# Revit family: IS_Extra_BD510_BIM_GB
name_source: partatom
category: Plumbing Fixtures
units: mm (PartAtom-declared; Revit-internal decimal feet)

## family parameters
Always vertical = No
Cut with Voids When Loaded = No
OmniClass Number = 23.45.55.17
OmniClass Title = Mixing Faucets
Part Type = Normal
Room Calculation Point = No
Round Connector Dimension = Use Diameter
Shared = No
Work Plane-Based = No

## types (4) — shared parameters
BIMobject category = Taps & Mixers
BIMobject category code = sanitary-taps-mixers
BIMobject main category = Sanitary
BIMobject main category code = sanitary
Brand url = http://www.idealstandard.co.uk
Date of publishing = 09/11/2022
Description = Basin built in wall mounted 220mm kit 2 - for combination with kit 1 A1313NU
Edition number = 1
IFC Classification = Sanitary Terminal
Installation instructions = https://www.idealstandard.co.uk
Manufacturer = Ideal Standard
Manufacturer name = Ideal Standard
Masterformat 2014 Code = 22 40 00
Masterformat 2014 Description = Plumbing Fixtures
Material main = Brass
NBS Reference Code = 45-35-70/371
NBS Reference Description = Water supply fittings for wash basins and troughs
NominalHeight = 108 mm
NominalLength = 230 mm
NominalWidth = 167 mm
OmniClass Code = 23-31 11 00
OmniClass Description = Faucets
Product Guid = 95e05450-5292-4f1d-a68c-7bc8d674b562
Product SKU = BD510
Product certification = https://www.idealstandard.co.uk
Product data url = https://bimobject.com
Product family = Extra
Product group = Taps & Mixers
Product name = Basin built in wall mounted 220mm kit 2 - for combination with kit 1 A1313NU
Product url = https://www.idealstandard.co.uk
QR code = http://bimobject.com
Size = 167 x 230 x 108 mm
Technical description = https://www.idealstandard.co.uk
UNSPSC Code = 301815
URL = https://www.idealstandard.co.uk
Uniclass 1.4 Code = Mixer taps
Uniclass 1.4 Description = L725111
Uniclass 2.0 Code = Ac_20_64_30
Uniclass 2.0 Description = Fitting
Uniclass 2015 Code = Pr_40_20_87_96
Uniclass 2015 Name = Washbasin manual water supply sets
Uniformat II Code = Plumbing Fixtures
Uniformat II Description = D2010
Youtube clip = https://www.youtube.com

## per-type parameters (varying)
| type | GTIN code | Model |
| BD510AA - Basin built in wall mounted 220mm kit 2 - for combination with kit 1 A1313NU - Chrome | https://3800861111368 | BD510AA |
| BD510A2 - Basin built in wall mounted 220mm kit 2 - for combination with kit 1 A1313NU - Brushed Gold | https://3800861111757 | BD510A2 |
| BD510A5 - Basin built in wall mounted 220mm kit 2 - for combination with kit 1 A1313NU - Magnetic Grey | https://3800861112143 | BD510A5 |
| BD510GN - Basin built in wall mounted 220mm kit 2 - for combination with kit 1 A1313NU - Stainless Steel | https://3800861112532 | BD510GN |

## geometry (parser evidence)
native form markers: Sweep x3
no freeform markers — native parametric forms only
